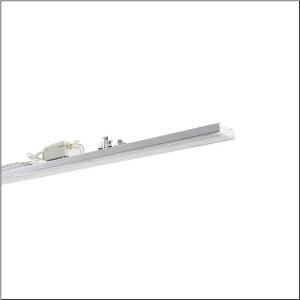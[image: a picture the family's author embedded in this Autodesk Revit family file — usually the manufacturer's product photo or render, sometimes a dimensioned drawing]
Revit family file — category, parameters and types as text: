
# Revit family: licross_r__21_recessed_mo_52te11cn49xg_3681
name_source: partatom
category: Lighting Fixtures
units: mm (PartAtom-declared; Revit-internal decimal feet)

## family parameters
Cut with Voids When Loaded = No
Host = Face
Light Source = No
Part Type = Normal
Room Calculation Point = No
Round Connector Dimension = Use Diameter
Shared = No

## types (1)
- --- (1 x LED, 9120 lm, 49.9 W, 4000K)
    Apparent Load = 50 VA
    CIE Flux Codes = 89 96 99 100 100
    Color Rendering = 80
    Color Temperature = 4000K
    Default Elevation = 1800 mm
    Description = Licross® 21 Recessed MO, luminaire insert, of sheet steel, galvanised, coil coated, white, length: 1.500mm, width: 66mm, height: 67mm, LED rated luminous flux: 9.120lm, light colour: 840, control gear: ON/OFF Multilumen, CLOi, control gear: ECG Multilumen, with plug, 3-pole, with phase selection, mains connection: 220..240V, AC, 50/60Hz, start of lifetime: 50W, end of service life: 61W, halogen-free wiring, primary light control with lens, of plastic, primary optical cover: cover, of PMMA, light emission: direct distribution, primary light characteristic: symmetric, protection rating (complete): IP54, insulation class (complete): insulation class I (protective earthing), certification: CE, ENEC, VDE, UKCA, protection symbol: D if used in an environment with non-conductive dust loads with corresponding accessories, impact resistance: IK06, permissible ambient temperature for indoor applications: -35..+40°C, corresponds to IFS (International Featured Standards) requirements for safety and quality in the food industry, reducing of maximum allowable ambient temperature of 5°C with ceiling mounting, LABS conformity tested according to VDMA 24364:2018-05, packaging unit: 1 piece
    Height = 58 mm
    Lamp = 1 x LED
    Lamp Light Flux = 9120 lm
    Lamp Power = 49.9 W
    Lamp count = 1
    Length = 1500 mm
    Luminous efficacy = 183 lm/W
    Manufacturer = Siteco
    ModVariant = No
    Model = 52TE11CN49XG
    Mounting Place = Ceiling
    Mounting Type = Pendant
    Number of Poles = 1
    OnlyDefault = Yes
    Power Factor = 1
    Product Name = Licross® 21 Recessed MO
    Product group = luminaire insert
    ProductGroupID = 901
    Protection Class = Protection class I
    Protection Degree = IP 54
    RLX_Detail_Level = 1
    RLX_Emergency_Light_Flux = 0 lm
    RLX_Emergency_Type = 0
    RLX_Emergency_Type_DB = No
    RlxData = <blob elided: 22289 chars, md5=0cdd777e>
    Socket = socket
    Standby Power = 0 W
    System Light Flux = 9120 lm
    System Power = 50 W
    Type Comments = factory setting: luminous flux: 100 % | (A | C | E) | 116 mA
    Type Image = l_1296930.jpg
    URL = http://relux.com
    VarID = @adj_040753
    Voltage = 0 V
    Weight = 0.00 kg
    Width = 66 mm

## geometry (parser evidence)
native form markers: Blend x4, Sweep x10
no freeform markers — native parametric forms only
